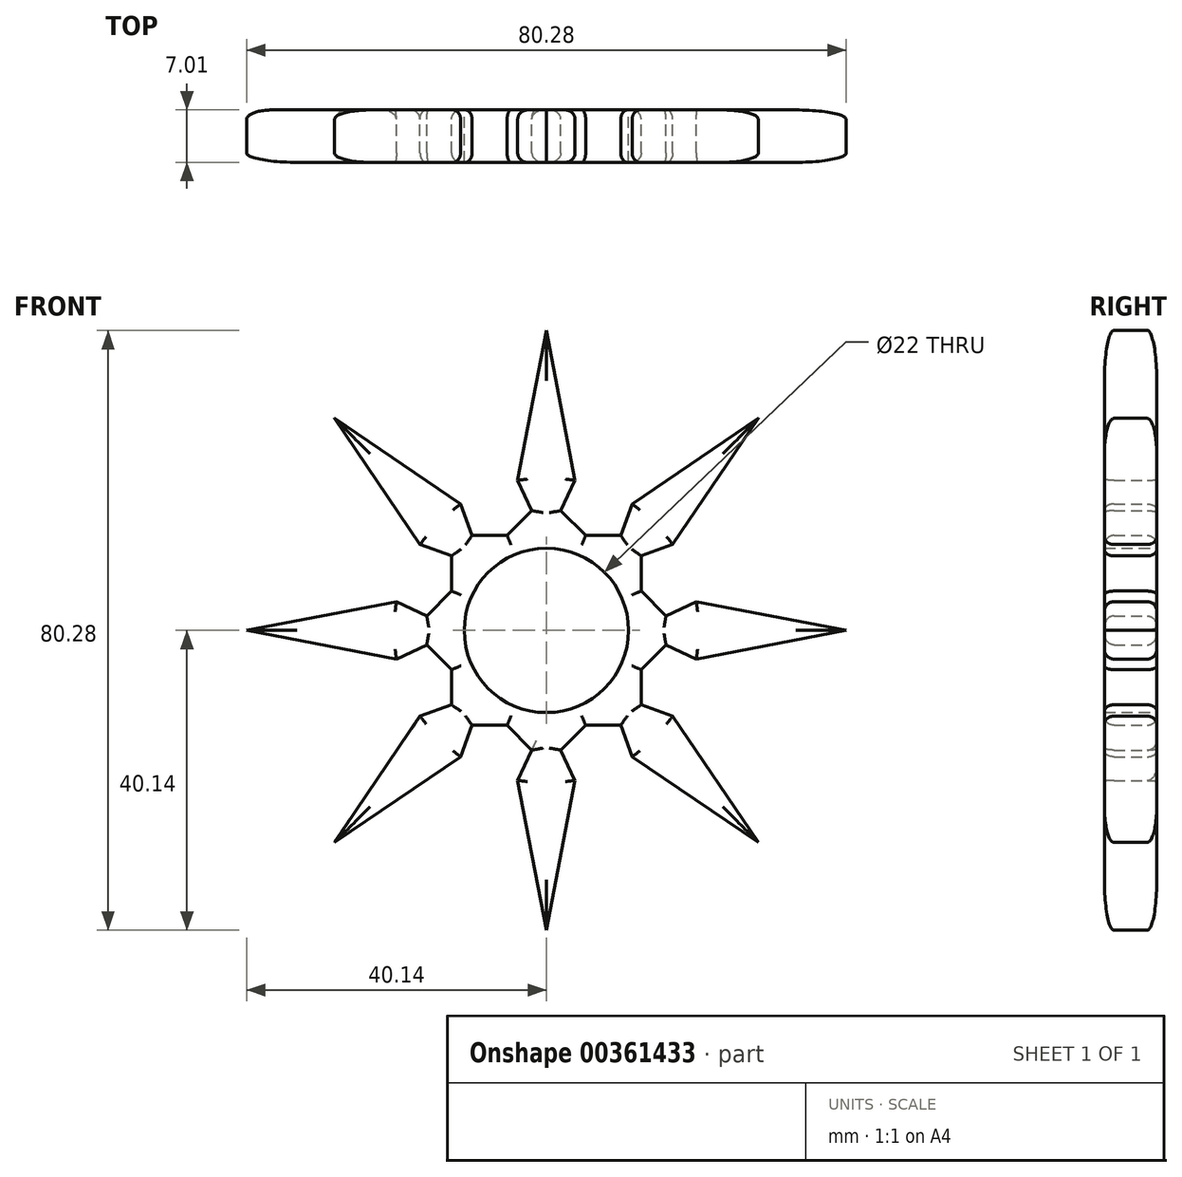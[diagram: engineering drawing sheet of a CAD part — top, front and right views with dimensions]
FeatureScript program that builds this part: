
annotation { "Feature Type Name" : "Feature", "Feature Type Description" : "" }
export const myFeature = defineFeature(function(context is Context, id is Id, definition is map)
    precondition{}
    {
        {
            var Q0;
            Q0=qCreatedBy(makeId("Front.planeOp"),FACE);
            var sketch = newSketch(context, id + "F0", { "sketchPlane" : qUnion([Q0])});
            skCircle(sketch, "E0.cCircle", {"center": v(0, 0) * mm, "radius": 12.7 * mm, "construction": true});
            skLineSegment(sketch, "E0.0", {"start": v(5.26, -12.7) * mm, "end": v(-5.26, -12.7) * mm});
            skLineSegment(sketch, "E0.1", {"start": v(-5.26, -12.7) * mm, "end": v(-12.7, -5.26) * mm});
            skLineSegment(sketch, "E0.2", {"start": v(-12.7, -5.26) * mm, "end": v(-12.7, 5.26) * mm});
            skLineSegment(sketch, "E0.3", {"start": v(-12.7, 5.26) * mm, "end": v(-5.26, 12.7) * mm});
            skLineSegment(sketch, "E0.4", {"start": v(-5.26, 12.7) * mm, "end": v(5.26, 12.7) * mm});
            skLineSegment(sketch, "E0.5", {"start": v(5.26, 12.7) * mm, "end": v(12.7, 5.26) * mm});
            skLineSegment(sketch, "E0.6", {"start": v(12.7, 5.26) * mm, "end": v(12.7, -5.26) * mm});
            skLineSegment(sketch, "E0.7", {"start": v(12.7, -5.26) * mm, "end": v(5.26, -12.7) * mm});
            skLineSegment(sketch, "E1", {"start": v(-5.26, 12.7) * mm, "end": v(0, 40.14) * mm});
            skLineSegment(sketch, "E2", {"start": v(0, 40.14) * mm, "end": v(5.26, 12.7) * mm});
            skCircle(sketch, "E3", {"center": v(0, 0) * mm, "radius": 11 * mm});
            skLineSegment(sketch, "E4", {"start": v(0, 0) * mm, "end": v(0, 5.52) * mm});
            skLineSegment(sketch, "E5", {"start": v(5.26, 12.7) * mm, "end": v(1.94, 16.02) * mm});
            skLineSegment(sketch, "E6", {"start": v(1.94, 16.02) * mm, "end": v(3.85, 20.08) * mm});
            skLineSegment(sketch, "E7.MirrorCS", {"start": v(-1.94, 16.02) * mm, "end": v(-3.85, 20.08) * mm});
            skLineSegment(sketch, "E8.MirrorCS", {"start": v(-5.26, 12.7) * mm, "end": v(-1.94, 16.02) * mm});
            skLineSegment(sketch, "E9.1.0", {"start": v(-28.38, 28.38) * mm, "end": v(-5.26, 12.7) * mm});
            skLineSegment(sketch, "E9.1.1", {"start": v(-12.7, 5.26) * mm, "end": v(-28.38, 28.38) * mm});
            skLineSegment(sketch, "E9.1.2", {"start": v(-12.7, 9.96) * mm, "end": v(-16.92, 11.48) * mm});
            skLineSegment(sketch, "E9.1.3", {"start": v(-9.96, 12.7) * mm, "end": v(-11.48, 16.92) * mm});
            skLineSegment(sketch, "E9.1.4", {"start": v(-5.26, 12.7) * mm, "end": v(-9.96, 12.7) * mm});
            skLineSegment(sketch, "E9.1.5", {"start": v(-12.7, 5.26) * mm, "end": v(-12.7, 9.96) * mm});
            skLineSegment(sketch, "E9.2.0", {"start": v(-40.14, 0) * mm, "end": v(-12.7, 5.26) * mm});
            skLineSegment(sketch, "E9.2.1", {"start": v(-12.7, -5.26) * mm, "end": v(-40.14, 0) * mm});
            skLineSegment(sketch, "E9.2.2", {"start": v(-16.02, -1.94) * mm, "end": v(-20.08, -3.85) * mm});
            skLineSegment(sketch, "E9.2.3", {"start": v(-16.02, 1.94) * mm, "end": v(-20.08, 3.85) * mm});
            skLineSegment(sketch, "E9.2.4", {"start": v(-12.7, 5.26) * mm, "end": v(-16.02, 1.94) * mm});
            skLineSegment(sketch, "E9.2.5", {"start": v(-12.7, -5.26) * mm, "end": v(-16.02, -1.94) * mm});
            skLineSegment(sketch, "E10.2.3.0", {"start": v(-28.38, -28.38) * mm, "end": v(-12.7, -5.26) * mm});
            skLineSegment(sketch, "E10.3.3.0", {"start": v(-5.26, -12.7) * mm, "end": v(-28.38, -28.38) * mm});
            skLineSegment(sketch, "E10.6.3.0", {"start": v(-9.96, -12.7) * mm, "end": v(-11.48, -16.92) * mm});
            skLineSegment(sketch, "E10.9.3.0", {"start": v(-12.7, -9.96) * mm, "end": v(-16.92, -11.48) * mm});
            skLineSegment(sketch, "E10.12.3.0", {"start": v(-12.7, -5.26) * mm, "end": v(-12.7, -9.96) * mm});
            skLineSegment(sketch, "E10.15.3.0", {"start": v(-5.26, -12.7) * mm, "end": v(-9.96, -12.7) * mm});
            skLineSegment(sketch, "E10.2.4.0", {"start": v(0, -40.14) * mm, "end": v(-5.26, -12.7) * mm});
            skLineSegment(sketch, "E10.3.4.0", {"start": v(5.26, -12.7) * mm, "end": v(0, -40.14) * mm});
            skLineSegment(sketch, "E10.6.4.0", {"start": v(1.94, -16.02) * mm, "end": v(3.85, -20.08) * mm});
            skLineSegment(sketch, "E10.9.4.0", {"start": v(-1.94, -16.02) * mm, "end": v(-3.85, -20.08) * mm});
            skLineSegment(sketch, "E10.12.4.0", {"start": v(-5.26, -12.7) * mm, "end": v(-1.94, -16.02) * mm});
            skLineSegment(sketch, "E10.15.4.0", {"start": v(5.26, -12.7) * mm, "end": v(1.94, -16.02) * mm});
            skLineSegment(sketch, "E10.2.5.0", {"start": v(28.38, -28.38) * mm, "end": v(5.26, -12.7) * mm});
            skLineSegment(sketch, "E10.3.5.0", {"start": v(12.7, -5.26) * mm, "end": v(28.38, -28.38) * mm});
            skLineSegment(sketch, "E10.6.5.0", {"start": v(12.7, -9.96) * mm, "end": v(16.92, -11.48) * mm});
            skLineSegment(sketch, "E10.9.5.0", {"start": v(9.96, -12.7) * mm, "end": v(11.48, -16.92) * mm});
            skLineSegment(sketch, "E10.12.5.0", {"start": v(5.26, -12.7) * mm, "end": v(9.96, -12.7) * mm});
            skLineSegment(sketch, "E10.15.5.0", {"start": v(12.7, -5.26) * mm, "end": v(12.7, -9.96) * mm});
            skLineSegment(sketch, "E10.2.6.0", {"start": v(40.14, 0) * mm, "end": v(12.7, -5.26) * mm});
            skLineSegment(sketch, "E10.3.6.0", {"start": v(12.7, 5.26) * mm, "end": v(40.14, 0) * mm});
            skLineSegment(sketch, "E10.6.6.0", {"start": v(16.02, 1.94) * mm, "end": v(20.08, 3.85) * mm});
            skLineSegment(sketch, "E10.9.6.0", {"start": v(16.02, -1.94) * mm, "end": v(20.08, -3.85) * mm});
            skLineSegment(sketch, "E10.12.6.0", {"start": v(12.7, -5.26) * mm, "end": v(16.02, -1.94) * mm});
            skLineSegment(sketch, "E10.15.6.0", {"start": v(12.7, 5.26) * mm, "end": v(16.02, 1.94) * mm});
            skLineSegment(sketch, "E10.2.7.0", {"start": v(28.38, 28.38) * mm, "end": v(12.7, 5.26) * mm});
            skLineSegment(sketch, "E10.3.7.0", {"start": v(5.26, 12.7) * mm, "end": v(28.38, 28.38) * mm});
            skLineSegment(sketch, "E10.6.7.0", {"start": v(9.96, 12.7) * mm, "end": v(11.48, 16.92) * mm});
            skLineSegment(sketch, "E10.9.7.0", {"start": v(12.7, 9.96) * mm, "end": v(16.92, 11.48) * mm});
            skLineSegment(sketch, "E10.12.7.0", {"start": v(12.7, 5.26) * mm, "end": v(12.7, 9.96) * mm});
            skLineSegment(sketch, "E10.15.7.0", {"start": v(5.26, 12.7) * mm, "end": v(9.96, 12.7) * mm});
            skSolve(sketch);
        }
        {
            var Q0;
            Q0=makeQuery(id+"F0.imprint","IMPRINT",FACE,{"disambiguationData":[TD([[makeQuery(id+"F0.imprint","IMPRINT",EDGE,{"derivedFrom":sQuery(id+"F0.wireOp",EDGE,"E0.3")}),1.0]])]});
            var Q1;
            Q1=makeQuery(id+"F0.imprint","IMPRINT",FACE,{"disambiguationData":[TD([[makeQuery(id+"F0.imprint","IMPRINT",EDGE,{"derivedFrom":sQuery(id+"F0.wireOp",EDGE,"E0.2")}),1.0]])]});
            var Q2;
            Q2=makeQuery(id+"F0.imprint","IMPRINT",FACE,{"disambiguationData":[TD([[makeQuery(id+"F0.imprint","IMPRINT",EDGE,{"derivedFrom":sQuery(id+"F0.wireOp",EDGE,"E0.1")}),1.0]])]});
            var Q3;
            Q3=makeQuery(id+"F0.imprint","IMPRINT",FACE,{"disambiguationData":[TD([[makeQuery(id+"F0.imprint","IMPRINT",EDGE,{"derivedFrom":sQuery(id+"F0.wireOp",EDGE,"E0.0")}),1.0]])]});
            var Q4;
            Q4=makeQuery(id+"F0.imprint","IMPRINT",FACE,{"disambiguationData":[TD([[makeQuery(id+"F0.imprint","IMPRINT",EDGE,{"derivedFrom":sQuery(id+"F0.wireOp",EDGE,"E0.7")}),1.0]])]});
            var Q5;
            Q5=makeQuery(id+"F0.imprint","IMPRINT",FACE,{"disambiguationData":[TD([[makeQuery(id+"F0.imprint","IMPRINT",EDGE,{"derivedFrom":sQuery(id+"F0.wireOp",EDGE,"E0.6")}),1.0]])]});
            var Q6;
            Q6=makeQuery(id+"F0.imprint","IMPRINT",FACE,{"disambiguationData":[TD([[makeQuery(id+"F0.imprint","IMPRINT",EDGE,{"derivedFrom":sQuery(id+"F0.wireOp",EDGE,"E0.5")}),1.0]])]});
            var Q7;
            Q7=makeQuery(id+"F0.imprint","IMPRINT",FACE,{"disambiguationData":[TD([[makeQuery(id+"F0.imprint","IMPRINT",EDGE,{"derivedFrom":sQuery(id+"F0.wireOp",EDGE,"E0.4")}),1.0]])]});
            var Q8;
            Q8=makeQuery(id+"F0.imprint","IMPRINT",FACE,{"disambiguationData":[TD([[makeQuery(id+"F0.imprint","IMPRINT",EDGE,{"derivedFrom":sQuery(id+"F0.wireOp",EDGE,"E0.0")}),-1.0]])]});
            extrude(context, id + "F1", {"entities" : qUnion([Q0, Q1, Q2, Q3, Q4, Q5, Q6, Q7, Q8]), "depth" : 7 * mm, "offsetDistance" : 25.4 * mm});
        }
        {
            var Q0;
            Q0=makeQuery(id+"F1.opExtrude","CAP_EDGE",EDGE,{"disambiguationData":[OSD([sQuery(id+"F0.wireOp",EDGE,"E10.2.4.0")])],"isStart":false});
            var Q1;
            Q1=makeQuery(id+"F1.opExtrude","CAP_EDGE",EDGE,{"disambiguationData":[OSD([sQuery(id+"F0.wireOp",EDGE,"E10.3.4.0")])],"isStart":false});
            var Q2;
            Q2=makeQuery(id+"F1.opExtrude","CAP_EDGE",EDGE,{"disambiguationData":[OSD([sQuery(id+"F0.wireOp",EDGE,"E10.6.4.0")])],"isStart":false});
            var Q3;
            Q3=makeQuery(id+"F1.opExtrude","CAP_EDGE",EDGE,{"disambiguationData":[OSD([sQuery(id+"F0.wireOp",EDGE,"E10.15.4.0")])],"isStart":false});
            var Q4;
            Q4=makeQuery(id+"F1.opExtrude","CAP_EDGE",EDGE,{"disambiguationData":[OSD([sQuery(id+"F0.wireOp",EDGE,"E10.12.5.0")])],"isStart":false});
            var Q5;
            Q5=makeQuery(id+"F1.opExtrude","CAP_EDGE",EDGE,{"disambiguationData":[OSD([sQuery(id+"F0.wireOp",EDGE,"E10.9.5.0")])],"isStart":false});
            var Q6;
            Q6=makeQuery(id+"F1.opExtrude","CAP_EDGE",EDGE,{"disambiguationData":[OSD([sQuery(id+"F0.wireOp",EDGE,"E10.2.5.0")])],"isStart":false});
            var Q7;
            Q7=makeQuery(id+"F1.opExtrude","CAP_EDGE",EDGE,{"disambiguationData":[OSD([sQuery(id+"F0.wireOp",EDGE,"E10.3.5.0")])],"isStart":false});
            var Q8;
            Q8=makeQuery(id+"F1.opExtrude","CAP_EDGE",EDGE,{"disambiguationData":[OSD([sQuery(id+"F0.wireOp",EDGE,"E10.6.5.0")])],"isStart":false});
            var Q9;
            Q9=makeQuery(id+"F1.opExtrude","CAP_EDGE",EDGE,{"disambiguationData":[OSD([sQuery(id+"F0.wireOp",EDGE,"E10.15.5.0")])],"isStart":false});
            var Q10;
            Q10=makeQuery(id+"F1.opExtrude","CAP_EDGE",EDGE,{"disambiguationData":[OSD([sQuery(id+"F0.wireOp",EDGE,"E10.12.6.0")])],"isStart":false});
            var Q11;
            Q11=makeQuery(id+"F1.opExtrude","CAP_EDGE",EDGE,{"disambiguationData":[OSD([sQuery(id+"F0.wireOp",EDGE,"E10.9.6.0")])],"isStart":false});
            var Q12;
            Q12=makeQuery(id+"F1.opExtrude","CAP_EDGE",EDGE,{"disambiguationData":[OSD([sQuery(id+"F0.wireOp",EDGE,"E10.2.6.0")])],"isStart":false});
            var Q13;
            Q13=makeQuery(id+"F1.opExtrude","CAP_EDGE",EDGE,{"disambiguationData":[OSD([sQuery(id+"F0.wireOp",EDGE,"E10.3.6.0")])],"isStart":false});
            var Q14;
            Q14=makeQuery(id+"F1.opExtrude","CAP_EDGE",EDGE,{"disambiguationData":[OSD([sQuery(id+"F0.wireOp",EDGE,"E10.6.6.0")])],"isStart":false});
            var Q15;
            Q15=makeQuery(id+"F1.opExtrude","CAP_EDGE",EDGE,{"disambiguationData":[OSD([sQuery(id+"F0.wireOp",EDGE,"E10.15.6.0")])],"isStart":false});
            var Q16;
            Q16=makeQuery(id+"F1.opExtrude","CAP_EDGE",EDGE,{"disambiguationData":[OSD([sQuery(id+"F0.wireOp",EDGE,"E10.12.7.0")])],"isStart":false});
            var Q17;
            Q17=makeQuery(id+"F1.opExtrude","CAP_EDGE",EDGE,{"disambiguationData":[OSD([sQuery(id+"F0.wireOp",EDGE,"E10.9.7.0")])],"isStart":false});
            var Q18;
            Q18=makeQuery(id+"F1.opExtrude","CAP_EDGE",EDGE,{"disambiguationData":[OSD([sQuery(id+"F0.wireOp",EDGE,"E10.2.7.0")])],"isStart":false});
            var Q19;
            Q19=makeQuery(id+"F1.opExtrude","CAP_EDGE",EDGE,{"disambiguationData":[OSD([sQuery(id+"F0.wireOp",EDGE,"E10.3.7.0")])],"isStart":false});
            var Q20;
            Q20=makeQuery(id+"F1.opExtrude","CAP_EDGE",EDGE,{"disambiguationData":[OSD([sQuery(id+"F0.wireOp",EDGE,"E10.6.7.0")])],"isStart":false});
            var Q21;
            Q21=makeQuery(id+"F1.opExtrude","CAP_EDGE",EDGE,{"disambiguationData":[OSD([sQuery(id+"F0.wireOp",EDGE,"E10.15.7.0")])],"isStart":false});
            var Q22;
            Q22=makeQuery(id+"F1.opExtrude","CAP_EDGE",EDGE,{"disambiguationData":[OSD([sQuery(id+"F0.wireOp",EDGE,"E5")])],"isStart":false});
            var Q23;
            Q23=makeQuery(id+"F1.opExtrude","CAP_EDGE",EDGE,{"disambiguationData":[OSD([sQuery(id+"F0.wireOp",EDGE,"E6")])],"isStart":false});
            var Q24;
            Q24=makeQuery(id+"F1.opExtrude","CAP_EDGE",EDGE,{"disambiguationData":[OSD([sQuery(id+"F0.wireOp",EDGE,"E2")])],"isStart":false});
            var Q25;
            Q25=makeQuery(id+"F1.opExtrude","CAP_EDGE",EDGE,{"disambiguationData":[OSD([sQuery(id+"F0.wireOp",EDGE,"E1")])],"isStart":false});
            var Q26;
            Q26=makeQuery(id+"F1.opExtrude","CAP_EDGE",EDGE,{"disambiguationData":[OSD([sQuery(id+"F0.wireOp",EDGE,"E7.MirrorCS")])],"isStart":false});
            var Q27;
            Q27=makeQuery(id+"F1.opExtrude","CAP_EDGE",EDGE,{"disambiguationData":[OSD([sQuery(id+"F0.wireOp",EDGE,"E8.MirrorCS")])],"isStart":false});
            var Q28;
            Q28=makeQuery(id+"F1.opExtrude","CAP_EDGE",EDGE,{"disambiguationData":[OSD([sQuery(id+"F0.wireOp",EDGE,"E9.1.4")])],"isStart":false});
            var Q29;
            Q29=makeQuery(id+"F1.opExtrude","CAP_EDGE",EDGE,{"disambiguationData":[OSD([sQuery(id+"F0.wireOp",EDGE,"E9.1.3")])],"isStart":false});
            var Q30;
            Q30=makeQuery(id+"F1.opExtrude","CAP_EDGE",EDGE,{"disambiguationData":[OSD([sQuery(id+"F0.wireOp",EDGE,"E9.1.0")])],"isStart":false});
            var Q31;
            Q31=makeQuery(id+"F1.opExtrude","CAP_EDGE",EDGE,{"disambiguationData":[OSD([sQuery(id+"F0.wireOp",EDGE,"E9.1.1")])],"isStart":false});
            var Q32;
            Q32=makeQuery(id+"F1.opExtrude","CAP_EDGE",EDGE,{"disambiguationData":[OSD([sQuery(id+"F0.wireOp",EDGE,"E9.1.2")])],"isStart":false});
            var Q33;
            Q33=makeQuery(id+"F1.opExtrude","CAP_EDGE",EDGE,{"disambiguationData":[OSD([sQuery(id+"F0.wireOp",EDGE,"E9.1.5")])],"isStart":false});
            var Q34;
            Q34=makeQuery(id+"F1.opExtrude","CAP_EDGE",EDGE,{"disambiguationData":[OSD([sQuery(id+"F0.wireOp",EDGE,"E9.2.4")])],"isStart":false});
            var Q35;
            Q35=makeQuery(id+"F1.opExtrude","CAP_EDGE",EDGE,{"disambiguationData":[OSD([sQuery(id+"F0.wireOp",EDGE,"E9.2.3")])],"isStart":false});
            var Q36;
            Q36=makeQuery(id+"F1.opExtrude","CAP_EDGE",EDGE,{"disambiguationData":[OSD([sQuery(id+"F0.wireOp",EDGE,"E9.2.0")])],"isStart":false});
            var Q37;
            Q37=makeQuery(id+"F1.opExtrude","CAP_EDGE",EDGE,{"disambiguationData":[OSD([sQuery(id+"F0.wireOp",EDGE,"E10.3.3.0")])],"isStart":false});
            var Q38;
            Q38=makeQuery(id+"F1.opExtrude","CAP_EDGE",EDGE,{"disambiguationData":[OSD([sQuery(id+"F0.wireOp",EDGE,"E10.6.3.0")])],"isStart":false});
            var Q39;
            Q39=makeQuery(id+"F1.opExtrude","CAP_EDGE",EDGE,{"disambiguationData":[OSD([sQuery(id+"F0.wireOp",EDGE,"E10.15.3.0")])],"isStart":false});
            var Q40;
            Q40=makeQuery(id+"F1.opExtrude","CAP_EDGE",EDGE,{"disambiguationData":[OSD([sQuery(id+"F0.wireOp",EDGE,"E10.12.4.0")])],"isStart":false});
            var Q41;
            Q41=makeQuery(id+"F1.opExtrude","CAP_EDGE",EDGE,{"disambiguationData":[OSD([sQuery(id+"F0.wireOp",EDGE,"E10.2.3.0")])],"isStart":false});
            var Q42;
            Q42=makeQuery(id+"F1.opExtrude","CAP_EDGE",EDGE,{"disambiguationData":[OSD([sQuery(id+"F0.wireOp",EDGE,"E10.9.3.0")])],"isStart":false});
            var Q43;
            Q43=makeQuery(id+"F1.opExtrude","CAP_EDGE",EDGE,{"disambiguationData":[OSD([sQuery(id+"F0.wireOp",EDGE,"E10.12.3.0")])],"isStart":false});
            var Q44;
            Q44=makeQuery(id+"F1.opExtrude","CAP_EDGE",EDGE,{"disambiguationData":[OSD([sQuery(id+"F0.wireOp",EDGE,"E9.2.5")])],"isStart":false});
            var Q45;
            Q45=makeQuery(id+"F1.opExtrude","CAP_EDGE",EDGE,{"disambiguationData":[OSD([sQuery(id+"F0.wireOp",EDGE,"E9.2.2")])],"isStart":false});
            var Q46;
            Q46=makeQuery(id+"F1.opExtrude","CAP_EDGE",EDGE,{"disambiguationData":[OSD([sQuery(id+"F0.wireOp",EDGE,"E9.2.1")])],"isStart":false});
            var Q47;
            Q47=makeQuery(id+"F1.opExtrude","CAP_EDGE",EDGE,{"disambiguationData":[OSD([sQuery(id+"F0.wireOp",EDGE,"E10.9.4.0")])],"isStart":false});
            fillet(context, id + "F2", {"entities" : qUnion([Q0, Q1, Q2, Q3, Q4, Q5, Q6, Q7, Q8, Q9, Q10, Q11, Q12, Q13, Q14, Q15, Q16, Q17, Q18, Q19, Q20, Q21, Q22, Q23, Q24, Q25, Q26, Q27, Q28, Q29, Q30, Q31, Q32, Q33, Q34, Q35, Q36, Q37, Q38, Q39, Q40, Q41, Q42, Q43, Q44, Q45, Q46, Q47]), "radius" : 1.27 * mm, "tangentPropagation" : true, "allowEdgeOverflow" : false});
        }
        {
            var Q0;
            Q0=makeQuery(id+"F1.opExtrude","CAP_EDGE",EDGE,{"disambiguationData":[OSD([sQuery(id+"F0.wireOp",EDGE,"E10.3.7.0")])],"isStart":true});
            var Q1;
            Q1=makeQuery(id+"F1.opExtrude","CAP_EDGE",EDGE,{"disambiguationData":[OSD([sQuery(id+"F0.wireOp",EDGE,"E10.2.7.0")])],"isStart":true});
            var Q2;
            Q2=makeQuery(id+"F1.opExtrude","CAP_EDGE",EDGE,{"disambiguationData":[OSD([sQuery(id+"F0.wireOp",EDGE,"E10.9.7.0")])],"isStart":true});
            var Q3;
            Q3=makeQuery(id+"F1.opExtrude","CAP_EDGE",EDGE,{"disambiguationData":[OSD([sQuery(id+"F0.wireOp",EDGE,"E10.6.7.0")])],"isStart":true});
            var Q4;
            Q4=makeQuery(id+"F1.opExtrude","CAP_EDGE",EDGE,{"disambiguationData":[OSD([sQuery(id+"F0.wireOp",EDGE,"E10.15.7.0")])],"isStart":true});
            var Q5;
            Q5=makeQuery(id+"F1.opExtrude","CAP_EDGE",EDGE,{"disambiguationData":[OSD([sQuery(id+"F0.wireOp",EDGE,"E5")])],"isStart":true});
            var Q6;
            Q6=makeQuery(id+"F1.opExtrude","CAP_EDGE",EDGE,{"disambiguationData":[OSD([sQuery(id+"F0.wireOp",EDGE,"E6")])],"isStart":true});
            var Q7;
            Q7=makeQuery(id+"F1.opExtrude","CAP_EDGE",EDGE,{"disambiguationData":[OSD([sQuery(id+"F0.wireOp",EDGE,"E2")])],"isStart":true});
            var Q8;
            Q8=makeQuery(id+"F1.opExtrude","CAP_EDGE",EDGE,{"disambiguationData":[OSD([sQuery(id+"F0.wireOp",EDGE,"E1")])],"isStart":true});
            var Q9;
            Q9=makeQuery(id+"F1.opExtrude","CAP_EDGE",EDGE,{"disambiguationData":[OSD([sQuery(id+"F0.wireOp",EDGE,"E7.MirrorCS")])],"isStart":true});
            var Q10;
            Q10=makeQuery(id+"F1.opExtrude","CAP_EDGE",EDGE,{"disambiguationData":[OSD([sQuery(id+"F0.wireOp",EDGE,"E8.MirrorCS")])],"isStart":true});
            var Q11;
            Q11=makeQuery(id+"F1.opExtrude","CAP_EDGE",EDGE,{"disambiguationData":[OSD([sQuery(id+"F0.wireOp",EDGE,"E9.1.4")])],"isStart":true});
            var Q12;
            Q12=makeQuery(id+"F1.opExtrude","CAP_EDGE",EDGE,{"disambiguationData":[OSD([sQuery(id+"F0.wireOp",EDGE,"E9.1.3")])],"isStart":true});
            var Q13;
            Q13=makeQuery(id+"F1.opExtrude","CAP_EDGE",EDGE,{"disambiguationData":[OSD([sQuery(id+"F0.wireOp",EDGE,"E9.1.0")])],"isStart":true});
            var Q14;
            Q14=makeQuery(id+"F1.opExtrude","CAP_EDGE",EDGE,{"disambiguationData":[OSD([sQuery(id+"F0.wireOp",EDGE,"E9.1.1")])],"isStart":true});
            var Q15;
            Q15=makeQuery(id+"F1.opExtrude","CAP_EDGE",EDGE,{"disambiguationData":[OSD([sQuery(id+"F0.wireOp",EDGE,"E9.1.2")])],"isStart":true});
            var Q16;
            Q16=makeQuery(id+"F1.opExtrude","CAP_EDGE",EDGE,{"disambiguationData":[OSD([sQuery(id+"F0.wireOp",EDGE,"E9.1.5")])],"isStart":true});
            var Q17;
            Q17=makeQuery(id+"F1.opExtrude","CAP_EDGE",EDGE,{"disambiguationData":[OSD([sQuery(id+"F0.wireOp",EDGE,"E9.2.4")])],"isStart":true});
            var Q18;
            Q18=makeQuery(id+"F1.opExtrude","CAP_EDGE",EDGE,{"disambiguationData":[OSD([sQuery(id+"F0.wireOp",EDGE,"E9.2.3")])],"isStart":true});
            var Q19;
            {var subQ0=sQuery(id+"F0.wireOp",EDGE,"E9.2.0");Q19=makeQuery(id+"F2.opFillet","BLEND_EDGE",EDGE,{"blendedFrom":[makeQuery(id+"F1.opExtrude","CAP_EDGE",EDGE,{"disambiguationData":[OSD([subQ0])],"isStart":false}),makeQuery(id+"F1.opExtrude","SWEPT_FACE",FACE,{"disambiguationData":[OSD([subQ0])]})],"blendedInto":[makeQuery(id+"F1.opExtrude","SWEPT_FACE",FACE,{"disambiguationData":[OSD([subQ0])]})]});}
            var Q20;
            Q20=makeQuery(id+"F1.opExtrude","CAP_EDGE",EDGE,{"disambiguationData":[OSD([sQuery(id+"F0.wireOp",EDGE,"E9.2.1")])],"isStart":true});
            var Q21;
            Q21=makeQuery(id+"F1.opExtrude","CAP_EDGE",EDGE,{"disambiguationData":[OSD([sQuery(id+"F0.wireOp",EDGE,"E9.2.2")])],"isStart":true});
            var Q22;
            Q22=makeQuery(id+"F1.opExtrude","CAP_EDGE",EDGE,{"disambiguationData":[OSD([sQuery(id+"F0.wireOp",EDGE,"E9.2.5")])],"isStart":true});
            var Q23;
            Q23=makeQuery(id+"F1.opExtrude","CAP_EDGE",EDGE,{"disambiguationData":[OSD([sQuery(id+"F0.wireOp",EDGE,"E10.12.3.0")])],"isStart":true});
            var Q24;
            Q24=makeQuery(id+"F1.opExtrude","CAP_EDGE",EDGE,{"disambiguationData":[OSD([sQuery(id+"F0.wireOp",EDGE,"E10.9.3.0")])],"isStart":true});
            var Q25;
            {var subQ0=sQuery(id+"F0.wireOp",EDGE,"E10.2.3.0");Q25=makeQuery(id+"F2.opFillet","BLEND_EDGE",EDGE,{"blendedFrom":[makeQuery(id+"F1.opExtrude","CAP_EDGE",EDGE,{"disambiguationData":[OSD([subQ0])],"isStart":false}),makeQuery(id+"F1.opExtrude","SWEPT_FACE",FACE,{"disambiguationData":[OSD([subQ0])]})],"blendedInto":[makeQuery(id+"F1.opExtrude","SWEPT_FACE",FACE,{"disambiguationData":[OSD([subQ0])]})]});}
            var Q26;
            Q26=makeQuery(id+"F1.opExtrude","CAP_EDGE",EDGE,{"disambiguationData":[OSD([sQuery(id+"F0.wireOp",EDGE,"E10.3.3.0")])],"isStart":true});
            var Q27;
            Q27=makeQuery(id+"F1.opExtrude","CAP_EDGE",EDGE,{"disambiguationData":[OSD([sQuery(id+"F0.wireOp",EDGE,"E10.6.3.0")])],"isStart":true});
            var Q28;
            Q28=makeQuery(id+"F1.opExtrude","CAP_EDGE",EDGE,{"disambiguationData":[OSD([sQuery(id+"F0.wireOp",EDGE,"E10.15.3.0")])],"isStart":true});
            var Q29;
            Q29=makeQuery(id+"F1.opExtrude","CAP_EDGE",EDGE,{"disambiguationData":[OSD([sQuery(id+"F0.wireOp",EDGE,"E10.12.4.0")])],"isStart":true});
            var Q30;
            {var subQ0=sQuery(id+"F0.wireOp",EDGE,"E10.9.4.0");Q30=makeQuery(id+"F2.opFillet","BLEND_EDGE",EDGE,{"blendedFrom":[makeQuery(id+"F1.opExtrude","CAP_EDGE",EDGE,{"disambiguationData":[OSD([subQ0])],"isStart":false}),makeQuery(id+"F1.opExtrude","SWEPT_FACE",FACE,{"disambiguationData":[OSD([subQ0])]})],"blendedInto":[makeQuery(id+"F1.opExtrude","SWEPT_FACE",FACE,{"disambiguationData":[OSD([subQ0])]})]});}
            var Q31;
            Q31=makeQuery(id+"F1.opExtrude","CAP_EDGE",EDGE,{"disambiguationData":[OSD([sQuery(id+"F0.wireOp",EDGE,"E10.2.4.0")])],"isStart":true});
            var Q32;
            Q32=makeQuery(id+"F1.opExtrude","CAP_EDGE",EDGE,{"disambiguationData":[OSD([sQuery(id+"F0.wireOp",EDGE,"E10.3.4.0")])],"isStart":true});
            var Q33;
            Q33=makeQuery(id+"F1.opExtrude","CAP_EDGE",EDGE,{"disambiguationData":[OSD([sQuery(id+"F0.wireOp",EDGE,"E10.6.4.0")])],"isStart":true});
            var Q34;
            Q34=makeQuery(id+"F1.opExtrude","CAP_EDGE",EDGE,{"disambiguationData":[OSD([sQuery(id+"F0.wireOp",EDGE,"E10.15.4.0")])],"isStart":true});
            var Q35;
            Q35=makeQuery(id+"F1.opExtrude","CAP_EDGE",EDGE,{"disambiguationData":[OSD([sQuery(id+"F0.wireOp",EDGE,"E10.12.5.0")])],"isStart":true});
            var Q36;
            Q36=makeQuery(id+"F1.opExtrude","CAP_EDGE",EDGE,{"disambiguationData":[OSD([sQuery(id+"F0.wireOp",EDGE,"E10.9.5.0")])],"isStart":true});
            var Q37;
            Q37=makeQuery(id+"F1.opExtrude","CAP_EDGE",EDGE,{"disambiguationData":[OSD([sQuery(id+"F0.wireOp",EDGE,"E10.2.5.0")])],"isStart":true});
            var Q38;
            Q38=makeQuery(id+"F1.opExtrude","CAP_EDGE",EDGE,{"disambiguationData":[OSD([sQuery(id+"F0.wireOp",EDGE,"E10.3.5.0")])],"isStart":true});
            var Q39;
            Q39=makeQuery(id+"F1.opExtrude","CAP_EDGE",EDGE,{"disambiguationData":[OSD([sQuery(id+"F0.wireOp",EDGE,"E10.6.5.0")])],"isStart":true});
            var Q40;
            Q40=makeQuery(id+"F1.opExtrude","CAP_EDGE",EDGE,{"disambiguationData":[OSD([sQuery(id+"F0.wireOp",EDGE,"E10.15.5.0")])],"isStart":true});
            var Q41;
            Q41=makeQuery(id+"F1.opExtrude","CAP_EDGE",EDGE,{"disambiguationData":[OSD([sQuery(id+"F0.wireOp",EDGE,"E10.12.6.0")])],"isStart":true});
            var Q42;
            Q42=makeQuery(id+"F1.opExtrude","CAP_EDGE",EDGE,{"disambiguationData":[OSD([sQuery(id+"F0.wireOp",EDGE,"E10.9.6.0")])],"isStart":true});
            var Q43;
            Q43=makeQuery(id+"F1.opExtrude","CAP_EDGE",EDGE,{"disambiguationData":[OSD([sQuery(id+"F0.wireOp",EDGE,"E10.2.6.0")])],"isStart":true});
            var Q44;
            Q44=makeQuery(id+"F1.opExtrude","CAP_EDGE",EDGE,{"disambiguationData":[OSD([sQuery(id+"F0.wireOp",EDGE,"E10.3.6.0")])],"isStart":true});
            var Q45;
            Q45=makeQuery(id+"F1.opExtrude","CAP_EDGE",EDGE,{"disambiguationData":[OSD([sQuery(id+"F0.wireOp",EDGE,"E10.6.6.0")])],"isStart":true});
            var Q46;
            Q46=makeQuery(id+"F1.opExtrude","CAP_EDGE",EDGE,{"disambiguationData":[OSD([sQuery(id+"F0.wireOp",EDGE,"E10.15.6.0")])],"isStart":true});
            var Q47;
            Q47=makeQuery(id+"F1.opExtrude","CAP_EDGE",EDGE,{"disambiguationData":[OSD([sQuery(id+"F0.wireOp",EDGE,"E10.12.7.0")])],"isStart":true});
            fillet(context, id + "F3", {"entities" : qUnion([Q0, Q1, Q2, Q3, Q4, Q5, Q6, Q7, Q8, Q9, Q10, Q11, Q12, Q13, Q14, Q15, Q16, Q17, Q18, Q19, Q20, Q21, Q22, Q23, Q24, Q25, Q26, Q27, Q28, Q29, Q30, Q31, Q32, Q33, Q34, Q35, Q36, Q37, Q38, Q39, Q40, Q41, Q42, Q43, Q44, Q45, Q46, Q47]), "radius" : 1.27 * mm, "tangentPropagation" : true, "allowEdgeOverflow" : false});
        }
    });
